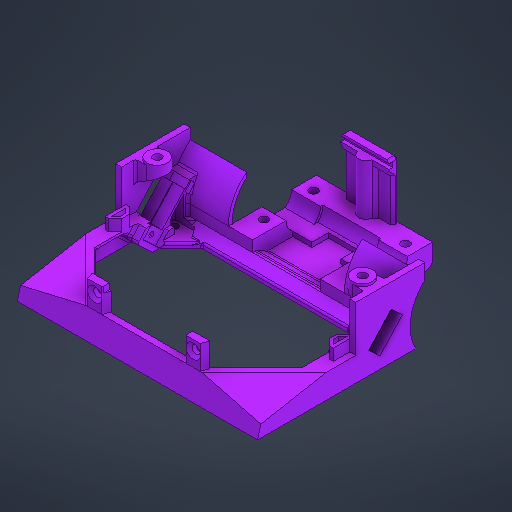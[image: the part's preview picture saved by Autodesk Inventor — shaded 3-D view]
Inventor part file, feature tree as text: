
AUTODESK INVENTOR PART (.ipt)
format: ipt  version: 2025 (Build 290162000, 162)  size: 1,826,304 bytes
history: native  units: mm
features: extrude x63, sketch x56, projected_geometry x55, other x6, fillet x5, chamfer x3, hole x3, mirror x1
ambient origin geometry x8: Origin, YZ Plane, XZ Plane, XY Plane, X Axis, Y Axis, Z Axis, Center Point
bodies: Body1 (feature_tree)
feature tree (192):
  other  "Těleso1"
  extrude  "Vysunutí1"  Depth=99.5mm
  extrude  "Vysunutí2"  Depth=67.5mm
  extrude  "Vysunutí3"  Depth=2.5mm
  extrude  "Vysunutí4"  Depth=10.0mm TaperAngle=0.0deg
  extrude  "Vysunutí5"  Depth=10.0mm TaperAngle=0.0deg
  extrude  "Vysunutí6"  Depth=5.0mm
  sketch  "Náčrt8"
  sketch  "Náčrt9"
  other  "Pracovní rovina1"
  extrude  "Vysunutí7"  TaperAngle=75.0deg  [1 undecoded]
  extrude  "Vysunutí8"  Depth=2.5mm
  extrude  "Vysunutí9"  Depth=10.0mm TaperAngle=0.0deg
  extrude  "Vysunutí10"  Depth=38.0mm
  sketch  "Náčrt15"
  extrude  "Vysunutí11"  Depth=19.0mm
  extrude  "Vysunutí12"  Depth=10.0mm TaperAngle=0.0deg
  extrude  "Vysunutí13"  Depth=1.0mm
  sketch  "Náčrt18"
  extrude  "Vysunutí14"  Depth=8.0mm
  extrude  "Vysunutí15"  Depth=10.0mm TaperAngle=0.0deg
  extrude  "Vysunutí16"  Depth=2.0mm
  extrude  "Vysunutí17"  Depth=10.0mm TaperAngle=0.0deg
  extrude  "Vysunutí19"  Depth=25.714466mm
  extrude  "Vysunutí48"  Depth=25.714466mm
  sketch  "Náčrt24"
  extrude  "Vysunutí20"  Depth=10.0mm TaperAngle=0.0deg
  extrude  "Vysunutí21"  Depth=1.5mm TaperAngle=0.0deg
  extrude  "Vysunutí29"  Depth=2.422mm
  extrude  "Vysunutí30"  Depth=1.5mm TaperAngle=0.0deg
  extrude  "Vysunutí31"  Depth=5.5mm
  sketch  "Náčrt34"
  extrude  "Vysunutí32"  Depth=7.5mm
  extrude  "Vysunutí33"  Depth=10.0mm TaperAngle=0.0deg
  extrude  "Vysunutí34"  Depth=15.5mm
  extrude  "Vysunutí74"  Depth=37.0mm
  sketch  "Náčrt36"
  sketch  "Náčrt37"
  extrude  "Vysunutí36"  Depth=1.5mm
  extrude  "Vysunutí37"  Depth=10.0mm TaperAngle=0.0deg
  extrude  "Vysunutí54"  Depth=9.0mm
  extrude  "Vysunutí39"  Depth=25.0mm TaperAngle=0.0deg
  chamfer  "Zkosení3"  Distance=6.0mm
  hole  "Díra1"  [1 undecoded]
  extrude  "Vysunutí40"  Depth=3.5mm
  extrude  "Vysunutí41"  Depth=2.5mm
  hole  "Díra3"  [1 undecoded]
  sketch  "Náčrt44"
  extrude  "Vysunutí42"  Depth=10.0mm
  extrude  "Vysunutí43"  Depth=3.5mm TaperAngle=0.0deg
  sketch  "Náčrt45"
  other  "Pracovní rovina2"
  sketch  "Náčrt46"
  extrude  "Vysunutí44"  Depth=1.0mm TaperAngle=0.0deg
  extrude  "Vysunutí45"  Depth=29.0mm
  extrude  "Vysunutí46"  Depth=9.0mm TaperAngle=0.0deg
  extrude  "Vysunutí47"  Depth=5.1mm
  sketch  "Náčrt54"
  extrude  "Vysunutí55"  Depth=16.5mm
  extrude  "Vysunutí56"  Depth=6.833mm
  extrude  "Vysunutí57"  Depth=9.0mm TaperAngle=0.0deg
  extrude  "Vysunutí58"  Depth=18.0mm
  extrude  "Vysunutí60"  Depth=10.0mm TaperAngle=0.0deg
  extrude  "Vysunutí59"  Depth=10.0mm TaperAngle=0.0deg
  sketch  "Náčrt57"
  other  "Pracovní rovina3"
  extrude  "Vysunutí62"  Depth=7.0mm TaperAngle=0.0deg
  extrude  "Vysunutí63"  Depth=14.0mm
  extrude  "Vysunutí64"  Depth=10.0mm
  extrude  "Vysunutí65"  Depth=3.5mm
  extrude  "Vysunutí66"  Depth=20.5mm
  other  "Pracovní rovina4"
  sketch  "Náčrt63"
  extrude  "Vysunutí67"  Depth=9.987mm
  extrude  "Vysunutí68"  Depth=10.0mm TaperAngle=0.0deg
  extrude  "Vysunutí84"  Depth=25.0mm
  extrude  "Vysunutí88"  Depth=2.5mm
  extrude  "Vysunutí85"  TaperAngle=45.0deg  [1 undecoded]
  extrude  "Vysunutí90"  Depth=10.0mm TaperAngle=0.0deg
  fillet  "Zaoblení6"  Radius=20.625mm
  fillet  "Zaoblení7"  Radius=5.0mm
  extrude  "Vysunutí108"  Depth=3.5mm
  other  "Pracovní rovina7"
  extrude  "Vysunutí110"  TaperAngle=0.0deg  [1 undecoded]
  mirror  "Zrcadlit1"
  sketch  "Náčrt99"
  extrude  "Vysunutí113"  Depth=3.5mm
  extrude  "Vysunutí111"  Depth=5.0mm
  extrude  "Vysunutí112"  Depth=41.0mm
  extrude  "Vysunutí89"  Depth=4.5mm TaperAngle=0.0deg
  fillet  "Zaoblení8"  Radius=4.0mm
  fillet  "Zaoblení9"  Radius=5.35mm
  fillet  "Zaoblení10"  Radius=2.5mm
  chamfer  "Zkosení11"  Distance=5.5mm
  hole  "Díra6"  [1 undecoded]
  chamfer  "Zkosení13"  Angle=60.0deg  [1 undecoded]
  sketch  "Náčrt2"
  sketch  "Náčrt3"
  sketch  "Náčrt4"
  sketch  "Náčrt5"
  sketch  "Náčrt6"
  sketch  "Náčrt7"
  sketch  "Náčrt10"
  sketch  "Náčrt11"
  projected_geometry  "Promítnutá smyčka1"
  sketch  "Náčrt13"
  projected_geometry  "Promítnutá smyčka3"
  sketch  "Náčrt14"
  projected_geometry  "Promítnutá smyčka4"
  sketch  "Náčrt16"
  projected_geometry  "Promítnutá smyčka5"
  sketch  "Náčrt20"
  sketch  "Náčrt21"
  sketch  "Náčrt23"
  projected_geometry  "Promítnutá smyčka8"
  projected_geometry  "Promítnutá smyčka9"
  projected_geometry  "Promítnutá smyčka10"
  projected_geometry  "Promítnutá smyčka11"
  projected_geometry  "Promítnutá smyčka12"
  sketch  "Náčrt31"
  sketch  "Náčrt32"
  sketch  "Náčrt33"
  projected_geometry  "Promítnutá smyčka21"
  sketch  "Náčrt35"
  projected_geometry  "Promítnutá smyčka22"
  projected_geometry  "Promítnutá smyčka23"
  projected_geometry  "Promítnutá smyčka24"
  sketch  "Náčrt39"
  sketch  "Náčrt40"
  sketch  "Náčrt41"
  projected_geometry  "Promítnutá smyčka28"
  sketch  "Náčrt43"
  projected_geometry  "Promítnutá smyčka30"
  projected_geometry  "Promítnutá smyčka31"
  projected_geometry  "Promítnutá smyčka32"
  projected_geometry  "Promítnutá smyčka33"
  projected_geometry  "Promítnutá smyčka34"
  sketch  "Náčrt47"
  projected_geometry  "Promítnutá smyčka35"
  projected_geometry  "Promítnutá smyčka36"
  projected_geometry  "Promítnutá smyčka37"
  projected_geometry  "Promítnutá smyčka38"
  sketch  "Náčrt48"
  projected_geometry  "Promítnutá smyčka39"
  sketch  "Náčrt49"
  projected_geometry  "Promítnutá smyčka40"
  sketch  "Náčrt53"
  projected_geometry  "Promítnutá smyčka44"
  projected_geometry  "Promítnutá smyčka45"
  projected_geometry  "Promítnutá smyčka46"
  projected_geometry  "Promítnutá smyčka47"
  projected_geometry  "Promítnutá smyčka48"
  sketch  "Náčrt55"
  projected_geometry  "Promítnutá smyčka49"
  sketch  "Náčrt58"
  projected_geometry  "Promítnutá smyčka51"
  projected_geometry  "Promítnutá smyčka52"
  projected_geometry  "Promítnutá smyčka53"
  sketch  "Náčrt59"
  projected_geometry  "Promítnutá smyčka54"
  projected_geometry  "Promítnutá smyčka55"
  sketch  "Náčrt60"
  projected_geometry  "Promítnutá smyčka56"
  sketch  "Náčrt61"
  projected_geometry  "Promítnutá smyčka57"
  sketch  "Náčrt62"
  projected_geometry  "Promítnutá smyčka58"
  projected_geometry  "Promítnutá smyčka59"
  projected_geometry  "Promítnutá smyčka60"
  projected_geometry  "Promítnutá smyčka61"
  sketch  "Náčrt67"
  projected_geometry  "Promítnutá smyčka64"
  sketch  "Náčrt73"
  projected_geometry  "Promítnutá smyčka74"
  sketch  "Náčrt74"
  projected_geometry  "Promítnutá smyčka75"
  sketch  "Náčrt77"
  projected_geometry  "Promítnutá smyčka78"
  projected_geometry  "Promítnutá smyčka79"
  projected_geometry  "Promítnutá smyčka80"
  projected_geometry  "Promítnutá smyčka81"
  projected_geometry  "Promítnutá smyčka82"
  projected_geometry  "Promítnutá smyčka83"
  projected_geometry  "Promítnutá smyčka84"
  sketch  "Náčrt78"
  projected_geometry  "Promítnutá smyčka85"
  sketch  "Náčrt79"
  projected_geometry  "Promítnutá smyčka86"
  sketch  "Náčrt96"
  sketch  "Náčrt98"
  projected_geometry  "Promítnutá smyčka122"
  sketch  "Náčrt100"
note: 7 required parameter values undecoded (feature->parameter linkage not recoverable at this tier; creation-order binding heuristic only, values carry confidence <= 0.55)
